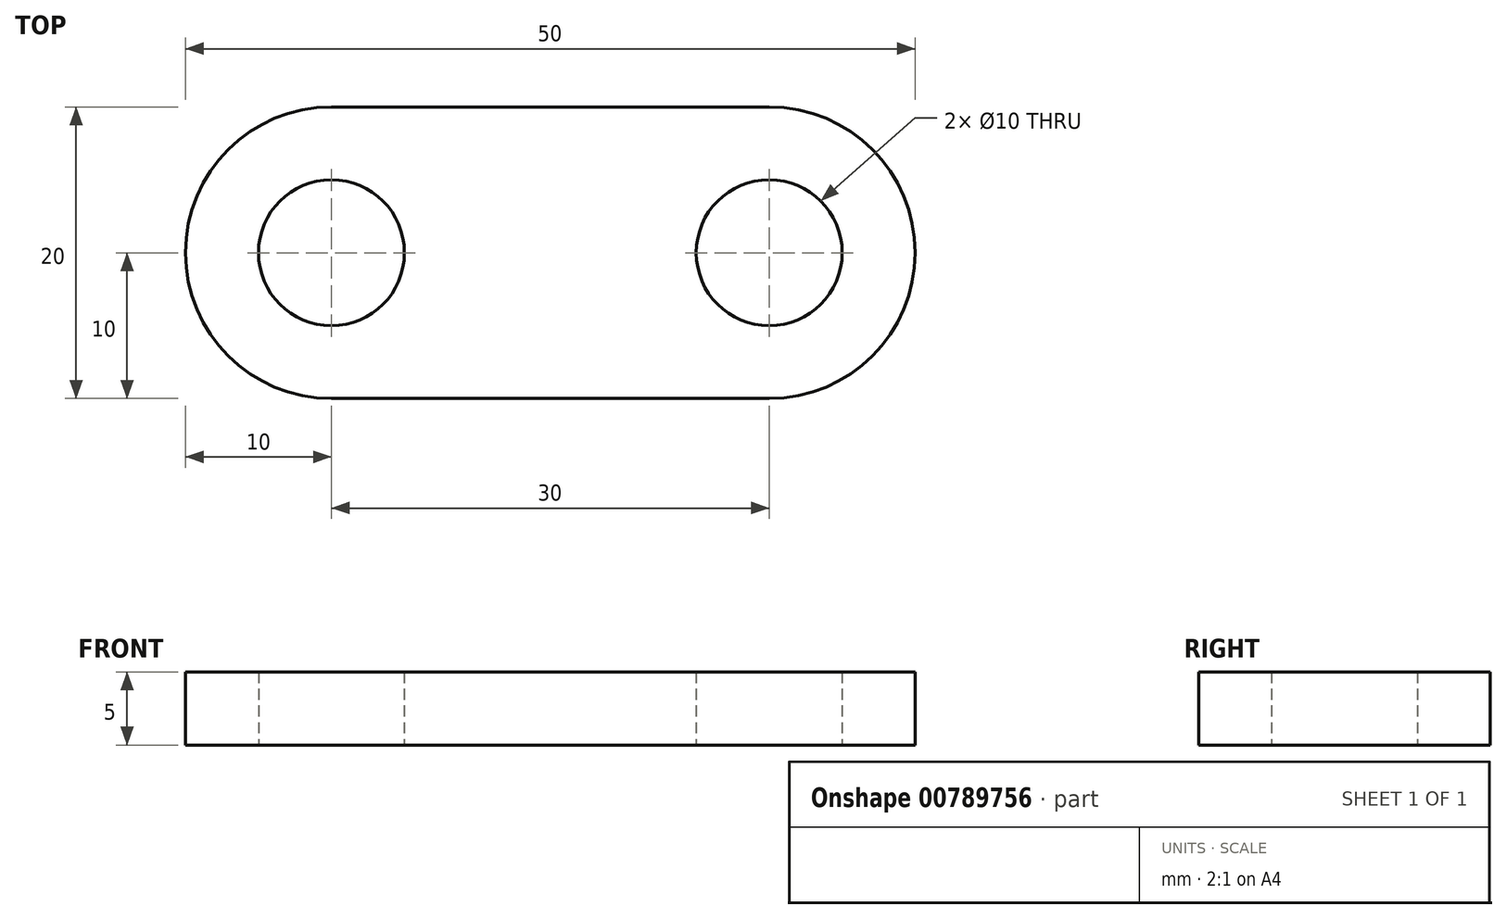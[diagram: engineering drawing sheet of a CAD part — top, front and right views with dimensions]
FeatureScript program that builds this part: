
annotation { "Feature Type Name" : "Feature", "Feature Type Description" : "" }
export const myFeature = defineFeature(function(context is Context, id is Id, definition is map)
    precondition{}
    {
        {
            var Q0;
            Q0=qCreatedBy(makeId("Top.planeOp"),FACE);
            var sketch = newSketch(context, id + "F0", { "sketchPlane" : qUnion([Q0])});
            skArc(sketch, "E0", {"start": v(0, 10) * mm, "mid": v(-10, 0) * mm, "end": v(0, -10) * mm});
            skArc(sketch, "E1", {"start": v(30, -10) * mm, "mid": v(40, 0) * mm, "end": v(30, 10) * mm});
            skLineSegment(sketch, "E2", {"start": v(0, -10) * mm, "end": v(30, -10) * mm});
            skLineSegment(sketch, "E3", {"start": v(0, 10) * mm, "end": v(30, 10) * mm});
            skCircle(sketch, "E4", {"center": v(0, 0) * mm, "radius": 5 * mm});
            skCircle(sketch, "E5", {"center": v(30, 0) * mm, "radius": 5 * mm});
            skSolve(sketch);
        }
        {
            var Q0;
            Q0=makeQuery(id+"F0.imprint","IMPRINT",FACE,{"disambiguationData":[TD([[makeQuery(id+"F0.imprint","IMPRINT",EDGE,{"derivedFrom":sQuery(id+"F0.wireOp",EDGE,"E0")}),1.0]])]});
            extrude(context, id + "F1", {"entities" : qUnion([Q0]), "depth" : 5 * mm, "offsetDistance" : 25 * mm});
        }
    });
